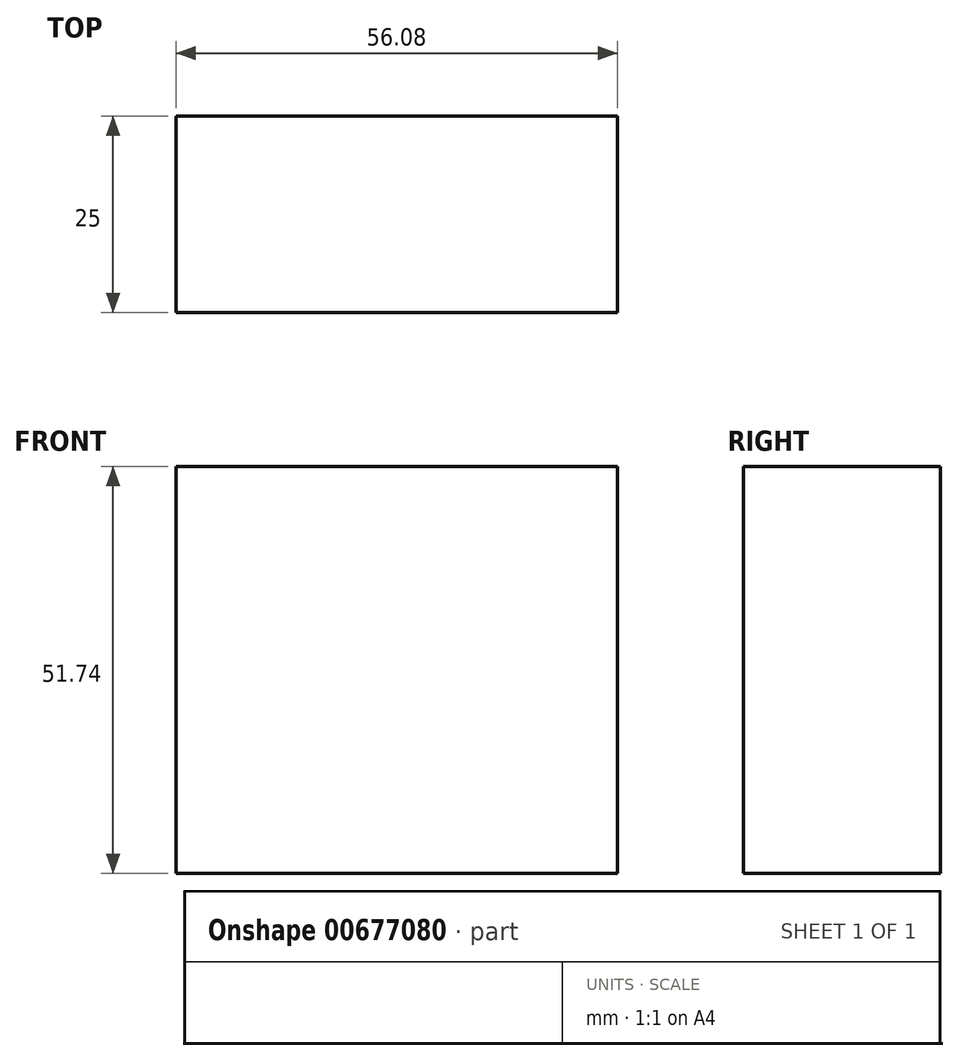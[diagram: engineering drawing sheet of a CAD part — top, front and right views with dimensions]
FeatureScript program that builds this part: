
annotation { "Feature Type Name" : "Feature", "Feature Type Description" : "" }
export const myFeature = defineFeature(function(context is Context, id is Id, definition is map)
    precondition{}
    {
        {
            var Q0;
            Q0=qCreatedBy(makeId("Front.planeOp"),FACE);
            var sketch = newSketch(context, id + "F0", { "sketchPlane" : qUnion([Q0])});
            skLineSegment(sketch, "E0.bottom", {"start": v(-66.63, -25.87) * mm, "end": v(-10.55, -25.87) * mm});
            skLineSegment(sketch, "E0.top", {"start": v(-66.63, 25.87) * mm, "end": v(-10.55, 25.87) * mm});
            skLineSegment(sketch, "E0.left", {"start": v(-66.63, -25.87) * mm, "end": v(-66.63, 25.87) * mm});
            skLineSegment(sketch, "E0.right", {"start": v(-10.55, -25.87) * mm, "end": v(-10.55, 25.87) * mm});
            skPoint(sketch, "E0.middle", {"position": v(-38.6, 0) * mm});
            skCircle(sketch, "E1", {"center": v(18.07, 0) * mm, "radius": 16.51 * mm});
            skSolve(sketch);
        }
        {
            var Q0;
            Q0=makeQuery(id+"F0.imprint","IMPRINT",FACE,{"disambiguationData":[TD([[makeQuery(id+"F0.imprint","IMPRINT",EDGE,{"derivedFrom":sQuery(id+"F0.wireOp",EDGE,"E0.bottom")}),1.0]])]});
            extrude(context, id + "F1", {"entities" : qUnion([Q0]), "depth" : 25 * mm, "offsetDistance" : 25 * mm});
        }
        {
            var Q0;
            Q0=makeQuery(id+"F1.opExtrude","CAP_FACE",FACE,{"disambiguationData":[OSD([sQuery(id+"F0.wireOp",EDGE,"E0.bottom"),sQuery(id+"F0.wireOp",EDGE,"E0.top"),sQuery(id+"F0.wireOp",EDGE,"E0.left"),sQuery(id+"F0.wireOp",EDGE,"E0.right")])],"isStart":false});
            var sketch = newSketch(context, id + "F2", { "sketchPlane" : qUnion([Q0])});
            skLineSegment(sketch, "E2", {"start": v(-56.95, 46.26) * mm, "end": v(-24.02, -42.61) * mm});
            skSolve(sketch);
        }
        {
            var Q0;
            Q0=sQuery(id+"F2.wireOp",EDGE,"E2");
            extrude(context, id + "F3", {"bodyType" : ToolBodyType.SURFACE, "surfaceEntities" : qUnion([Q0]), "depth" : 25 * mm, "offsetDistance" : 25 * mm});
        }
    });
